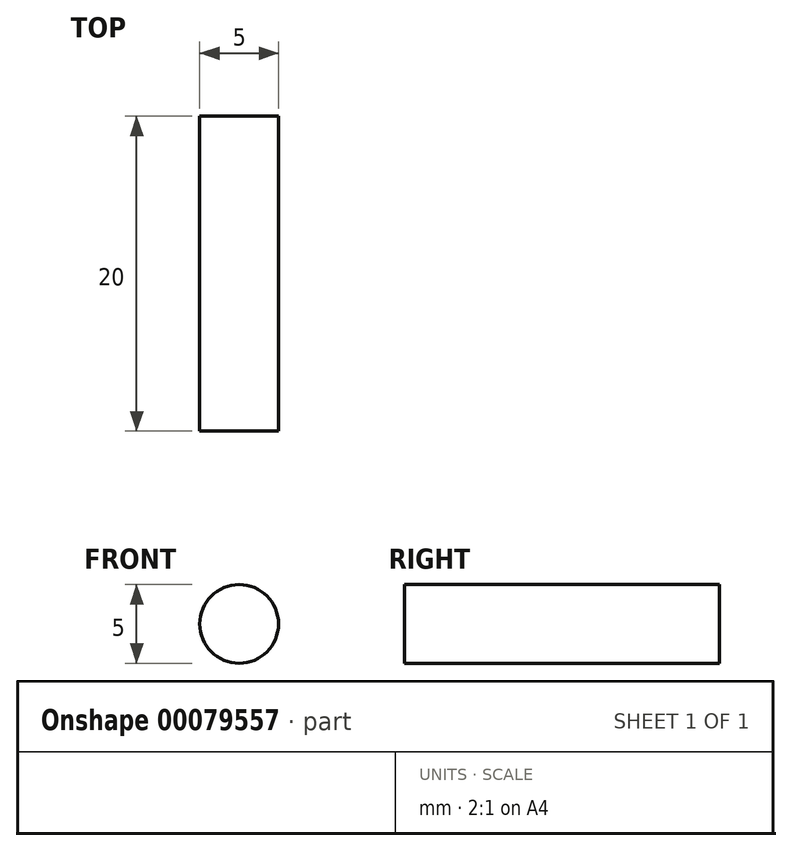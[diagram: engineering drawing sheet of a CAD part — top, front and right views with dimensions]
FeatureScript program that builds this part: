
annotation { "Feature Type Name" : "Feature", "Feature Type Description" : "" }
export const myFeature = defineFeature(function(context is Context, id is Id, definition is map)
    precondition{}
    {
        {
            var Q0;
            Q0=qCreatedBy(makeId("Front.planeOp"),FACE);
            var sketch = newSketch(context, id + "F0", { "sketchPlane" : qUnion([Q0])});
            skCircle(sketch, "E0", {"center": v(0, 0) * mm, "radius": 2.5 * mm});
            skSolve(sketch);
        }
        {
            var Q0;
            Q0=makeQuery(id+"F0.imprint","IMPRINT",FACE,{"disambiguationData":[TD([[makeQuery(id+"F0.imprint","IMPRINT",EDGE,{"derivedFrom":sQuery(id+"F0.wireOp",EDGE,"E0")}),1.0]])]});
            extrude(context, id + "F1", {"entities" : qUnion([Q0]), "depth" : 10 * mm, "hasSecondDirection" : true, "secondDirectionOppositeDirection" : true, "secondDirectionDepth" : 10 * mm});
        }
    });
